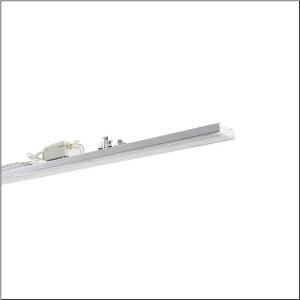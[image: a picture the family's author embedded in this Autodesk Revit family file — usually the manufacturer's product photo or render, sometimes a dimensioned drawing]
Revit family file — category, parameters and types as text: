
# Revit family: licross_21_recessed_ho_52te12dv4l2md
name_source: partatom
category: Lighting Fixtures
units: mm (PartAtom-declared; Revit-internal decimal feet)

## family parameters
Cut with Voids When Loaded = No
Host = Face
Light Source = No
Part Type = Normal
Room Calculation Point = No
Round Connector Dimension = Use Diameter
Shared = No

## types (1)
- --- (1 x LED, 22710 lm, 125.6 W, 4000K)
    Apparent Load = 126 VA
    CIE Flux Codes = 69 91 98 100 100
    Color Rendering = 80
    Color Temperature = 4000K
    Default Elevation = 1800 mm
    Description = Licross 21 Recessed HO, luminaire insert, of sheet steel, galvanised, coil coated, white, length: 2.250mm, width: 66mm, height: 67mm, LED rated luminous flux: 22.710lm, light colour: 840, SDCM (Standard Deviation of Colour Matching)MacAdam ≤ 3 SDCM (initial), control gear: DALI 2 (for two DALI lines), with plug, 6-pole, with phase selection, mains connection: 220..240V, AC/DC, 0/50..60Hz, rated input power: 126W, without changeover relay, for emergency light function, for central battery installations according to EN 60598-2-22, internal wiring halogen-free, primary optical cover: cover, of PMMA, light emission: direct distribution, primary light characteristic: symmetric, protection rating (complete): IP54, insulation class (complete): insulation class I (protective earthing), certification: CE, ENEC, VDE, UKCA, protection symbol: D if used in an environment with non-conductive dust loads with corresponding accessories, impact resistance: IK06, permissible ambient temperature for indoor applications: -40..+30°C, standard: EN 60598-2-22, corresponds to IFS (International Featured Standards) requirements for safety and quality in the food industry, reducing of maximum allowable ambient temperature of 5°C with ceiling mounting, LABS conformity tested according to VDMA 24364:2018-05, The light source and the operating device comply with the requirements of the Ecodesign Regulation (EU) 2019/2020 and are replaceable in accordance with this regulation, packaging unit: 1 piece
    Height = 58 mm
    Lamp = 1 x LED
    Lamp Light Flux = 22710 lm
    Lamp Power = 125.6 W
    Lamp count = 1
    Length = 2250 mm
    Luminous efficacy = 181 lm/W
    Manufacturer = Siteco
    ModVariant = No
    Model = 52TE12DV4L2MD
    Mounting Place = Ceiling
    Mounting Type = Pendant
    Number of Poles = 1
    OnlyDefault = Yes
    Power Factor = 1
    Product Name = Licross 21 Recessed HO
    Product group = luminaire insert | ceiling pendant
    ProductGroupID = 901
    Protection Class = Protection class I
    Protection Degree = IP 54
    RLX_Detail_Level = 1
    RLX_Emergency_Light_Flux = 0 lm
    RLX_Emergency_Type = 0
    RLX_Emergency_Type_DB = No
    RlxData = <blob elided: 30409 chars, md5=138307ae>
    Socket = socket
    Standby Power = 0 W
    System Light Flux = 22710 lm
    System Power = 126 W
    Type Comments = : AC-mode, luminous flux: 100 % | dim-lin: 254 | 489 mA
    Type Image = l_1296930.jpg
    URL = http://relux.com
    VarID = @adj_113185
    Voltage = 0 V
    Weight = 0.00 kg
    Width = 66 mm

## geometry (parser evidence)
native form markers: Blend x4, Sweep x10
no freeform markers — native parametric forms only
